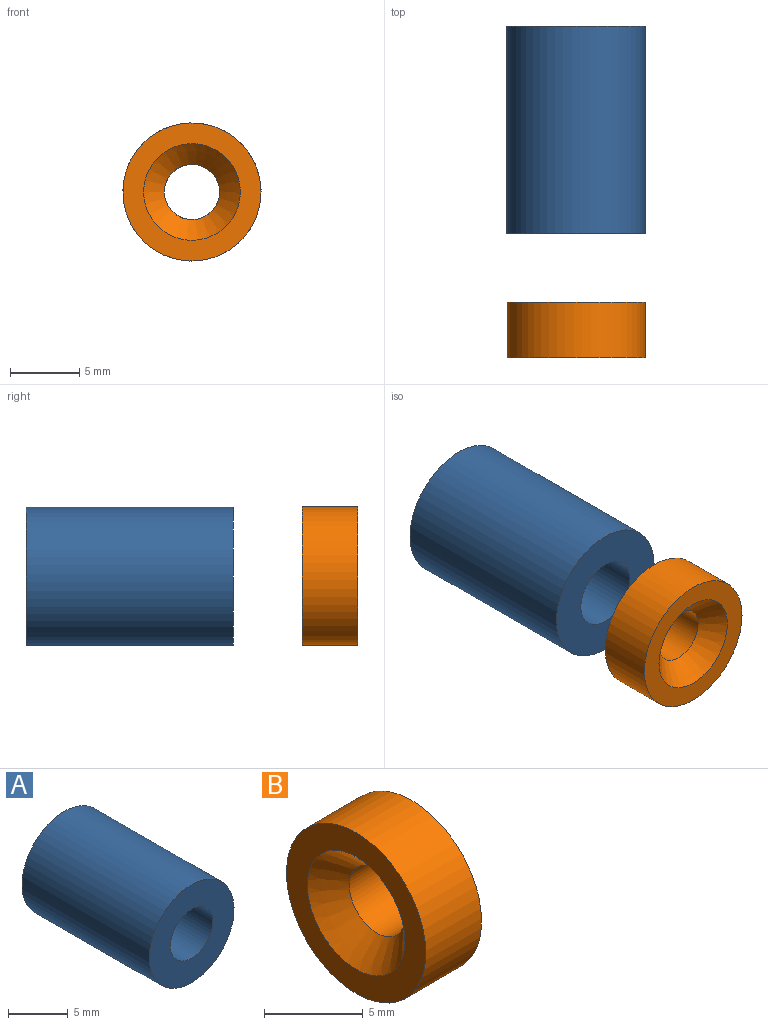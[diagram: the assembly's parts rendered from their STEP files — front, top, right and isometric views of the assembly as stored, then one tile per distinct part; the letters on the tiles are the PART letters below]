
ASSEMBLY  parts=2 mates=1
PART A: 4 faces, bbox 10x15x10 mm
  f0: cylinder r=5mm len=15mm, axis (0,1,0), area 471.2mm2, adj f1,f2
  f1: plane 10x10mm, normal (0,-1,0), area 58.9mm2, adj f0,f3
  f2: plane 10x10mm, normal (0,1,0), area 58.9mm2, adj f0,f3
  f3: cylinder r=2.5mm len=15mm, axis (0,-1,0), area 235.6mm2, adj f1,f2
PART B: 5 faces, bbox 4x10x10 mm
  f0: cylinder r=5mm len=10mm, axis (-1,0,0), area 125.7mm2, adj f1,f2
  f1: plane 10x10mm, normal (1,0,0), area 66mm2, adj f0,f3
  f2: plane 10x10mm, normal (-1,0,0), area 40.1mm2, adj f0,f4
  f3: cylinder r=2mm len=4mm, axis (-1,0,0), area 31.4mm2, adj f1,f4
  f4: cone r=2mm half-angle=45deg, axis (-1,0,0), area 36.7mm2, adj f2,f3
PLACE A t=(-1.73,6.49,-0.01)mm
PLACE B rot(axis=(-0.58,-0.58,0.58),120deg) t=(-1.73,-17.51,-0.01)mm
MATE cylindrical B.f3 <-> A.f3  axis (0,1,0) through (-1.73,-13.51,-0.01)mm
